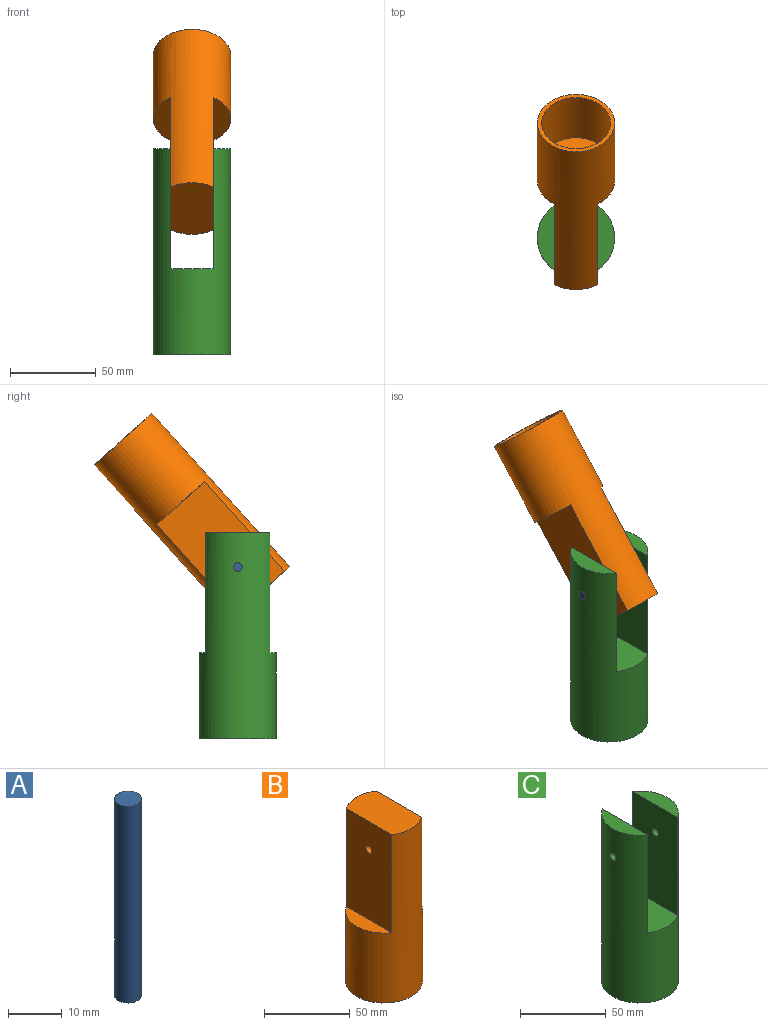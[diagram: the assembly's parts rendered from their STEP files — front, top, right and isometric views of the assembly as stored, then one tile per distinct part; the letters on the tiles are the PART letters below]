
ASSEMBLY  parts=3 mates=2
PART A: 3 faces, bbox 5x5x45 mm
  f0: cylinder r=2.5mm len=45mm, axis (0,0,-1), area 706.9mm2, adj f1,f2
  f1: plane 5x5mm, normal (0,0,1), area 19.6mm2, adj f0
  f2: plane 5x5mm, normal (0,0,-1), area 19.6mm2, adj f0
PART B: 10 faces, bbox 45x45x120 mm
  f0: plane 45x25mm, normal (0,0,1), area 1064.1mm2, adj f1,f3,f5
  f1: cylinder r=22.5mm len=120mm, axis (0,0,-1), area 10779.5mm2, adj f0,f2,f3,f4,f5,f6
  f2: plane 45x45mm, normal (0,0,-1), area 333.8mm2, adj f1,f7
  f3: plane 70x37.42mm, normal (1,0,0), area 2599.5mm2, adj f0,f1,f4,f9
  f4: plane 37.42x10mm, normal (0,0,1), area 263.2mm2, adj f1,f3
  f5: plane 70x37.42mm, normal (-1,0,0), area 2599.5mm2, adj f0,f1,f6,f9
  f6: plane 37.42x10mm, normal (0,0,1), area 263.2mm2, adj f1,f5
  f7: cylinder r=20mm len=40mm, axis (0,0,-1), area 4398.2mm2, adj f2,f8
  f8: plane 40x40mm, normal (0,0,-1), area 1256.6mm2, adj f7
  f9: cylinder r=2.5mm len=25mm, axis (1,0,0), area 392.7mm2, adj f3,f5
PART C: 11 faces, bbox 45x45x120 mm
  f0: cylinder r=22.5mm len=120mm, axis (0,0,-1), area 13214.5mm2, adj f1,f2,f3,f4,f5,f6,f9,f10
  f1: plane 37.42x10mm, normal (0,0,1), area 263.2mm2, adj f0,f4
  f2: plane 37.42x10mm, normal (0,0,1), area 263.2mm2, adj f0,f5
  f3: plane 45x45mm, normal (0,0,-1), area 333.8mm2, adj f0,f7
  f4: plane 70x37.42mm, normal (-1,0,0), area 2599.5mm2, adj f0,f1,f6,f10
  f5: plane 70x37.42mm, normal (1,0,0), area 2599.5mm2, adj f0,f2,f6,f9
  f6: plane 45x25mm, normal (0,0,1), area 1064.1mm2, adj f0,f4,f5
  f7: cylinder r=20mm len=40mm, axis (0,0,-1), area 4398.2mm2, adj f3,f8
  f8: plane 40x40mm, normal (0,0,-1), area 1256.6mm2, adj f7
  f9: cylinder r=2.5mm len=10mm, axis (1,0,0), area 156mm2, adj f0,f5
  f10: cylinder r=2.5mm len=10mm, axis (1,0,0), area 156mm2, adj f0,f4
PLACE A rot(axis=(0,1,0),90deg) t=(-84.32,-7.09,82.96)mm
PLACE B rot(axis=(1,0,0),138.1deg) t=(-61.82,59.65,157.43)mm
PLACE C t=(-61.89,-7.09,-17.04)mm fixed
MATE revolute A.f0 <-> B.f9  axis (-1,0,0) through (-61.82,-7.09,82.96)mm
MATE fastened C.f9 <-> A.f0  axis (1,0,0) through (-39.32,-7.09,82.96)mm
